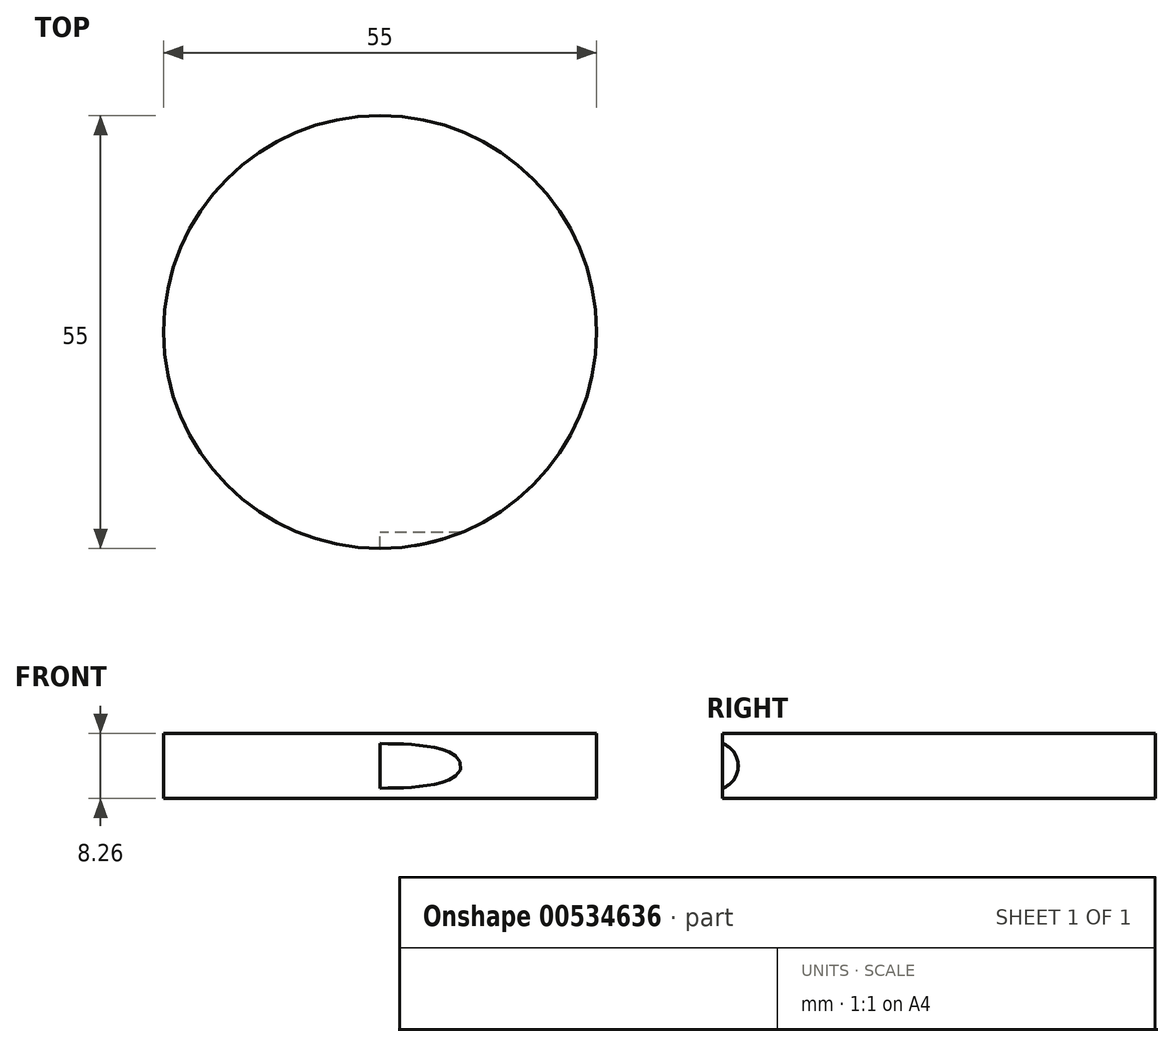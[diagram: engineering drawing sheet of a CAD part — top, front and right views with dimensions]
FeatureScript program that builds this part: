
annotation { "Feature Type Name" : "Feature", "Feature Type Description" : "" }
export const myFeature = defineFeature(function(context is Context, id is Id, definition is map)
    precondition{}
    {
        {
            var Q0;
            Q0=qCreatedBy(makeId("Top.planeOp"),FACE);
            var sketch = newSketch(context, id + "F0", { "sketchPlane" : qUnion([Q0])});
            skCircle(sketch, "E0", {"center": v(0, 0) * mm, "radius": 27.5 * mm});
            skSolve(sketch);
        }
        {
            var Q0;
            Q0 = qSketchRegion(id + "F0", true);
            extrude(context, id + "F1", {"entities" : qUnion([Q0]), "endBound" : BoundingType.SYMMETRIC, "depth" : 8.25 * mm, "offsetDistance" : 25 * mm});
        }
        {
            var Q0;
            Q0=qCreatedBy(makeId("Right.planeOp"),FACE);
            var sketch = newSketch(context, id + "F2", { "sketchPlane" : qUnion([Q0])});
            skCircle(sketch, "E1", {"center": v(-28.5, 0) * mm, "radius": 3 * mm});
            skSolve(sketch);
        }
        {
            var Q0;
            Q0=makeQuery(id+"F2.imprint","IMPRINT",FACE,{"disambiguationData":[TD([[makeQuery(id+"F2.imprint","IMPRINT",EDGE,{"derivedFrom":sQuery(id+"F2.wireOp",EDGE,"E1")}),1.0]])]});
            var Q1;
            Q1=sQuery(id+"F2.wireOp",EDGE,"E1");
            extrude(context, id + "F3", {"entities" : qUnion([Q0]), "operationType" : NewBodyOperationType.REMOVE, "surfaceEntities" : qUnion([Q1]), "depth" : 25 * mm, "offsetDistance" : 25 * mm});
        }
    });
